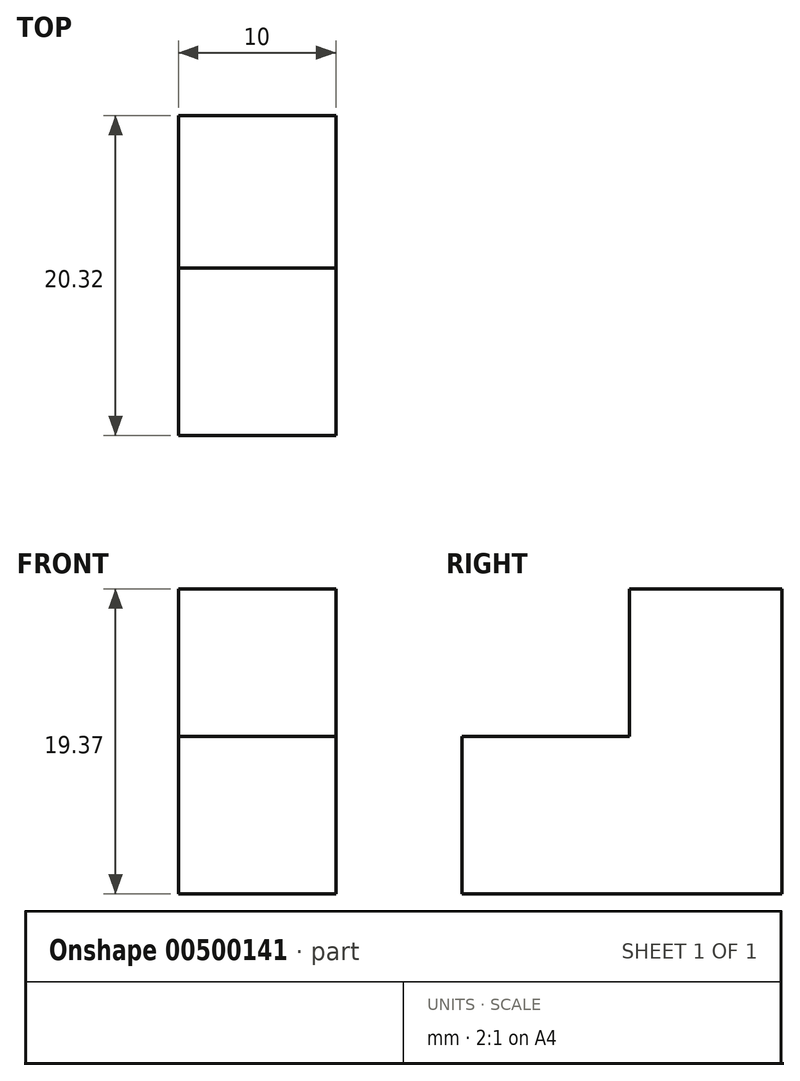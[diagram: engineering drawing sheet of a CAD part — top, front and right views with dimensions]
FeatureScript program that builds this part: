
annotation { "Feature Type Name" : "Feature", "Feature Type Description" : "" }
export const myFeature = defineFeature(function(context is Context, id is Id, definition is map)
    precondition{}
    {
        {
            var Q0;
            Q0=qCreatedBy(makeId("Right.planeOp"),FACE);
            var sketch = newSketch(context, id + "F0", { "sketchPlane" : qUnion([Q0])});
            skLineSegment(sketch, "E0", {"start": v(0, 0) * mm, "end": v(20.32, 0) * mm});
            skLineSegment(sketch, "E1", {"start": v(20.32, 0) * mm, "end": v(20.32, 19.37) * mm});
            skLineSegment(sketch, "E2", {"start": v(20.32, 19.37) * mm, "end": v(10.63, 19.37) * mm});
            skLineSegment(sketch, "E3", {"start": v(10.63, 19.37) * mm, "end": v(10.63, 10) * mm});
            skLineSegment(sketch, "E4", {"start": v(10.63, 10) * mm, "end": v(0, 10) * mm});
            skLineSegment(sketch, "E5", {"start": v(0, 10) * mm, "end": v(0, 0) * mm});
            skSolve(sketch);
        }
        {
            var Q0;
            Q0=makeQuery(id+"F0.imprint","IMPRINT",FACE,{"disambiguationData":[TD([[makeQuery(id+"F0.imprint","IMPRINT",EDGE,{"derivedFrom":sQuery(id+"F0.wireOp",EDGE,"E0")}),1.0]])]});
            extrude(context, id + "F1", {"entities" : qUnion([Q0]), "depth" : 10 * mm});
        }
    });
